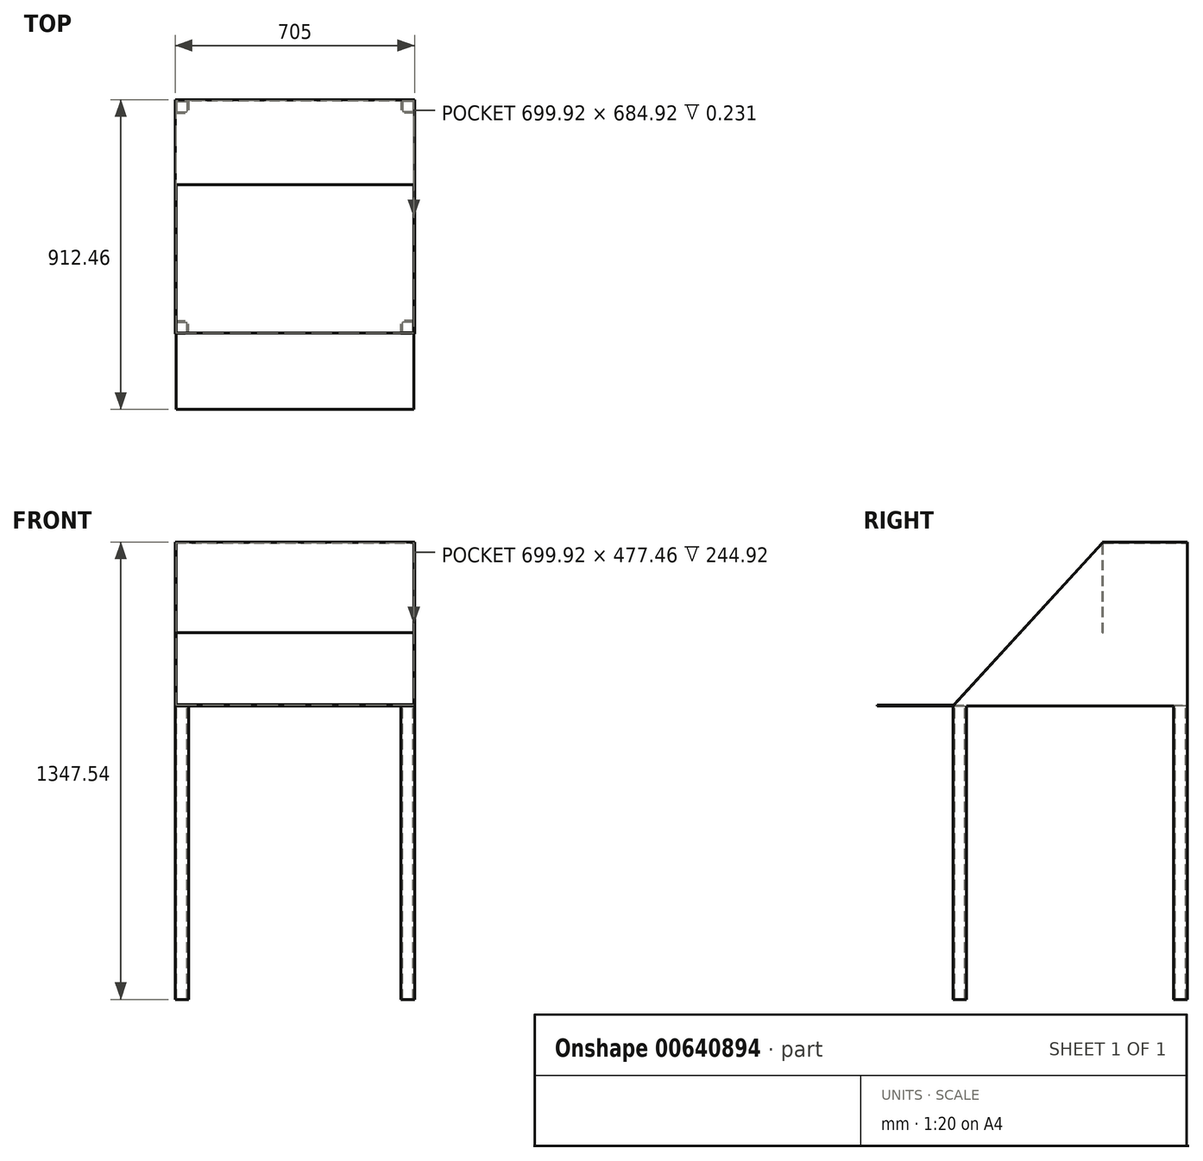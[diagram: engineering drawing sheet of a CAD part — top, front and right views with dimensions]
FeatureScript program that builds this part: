
annotation { "Feature Type Name" : "Feature", "Feature Type Description" : "" }
export const myFeature = defineFeature(function(context is Context, id is Id, definition is map)
    precondition{}
    {
        {
            var Q0;
            Q0=qCreatedBy(makeId("Front.planeOp"),FACE);
            var sketch = newSketch(context, id + "F0", { "sketchPlane" : qUnion([Q0])});
            skLineSegment(sketch, "E0.bottom", {"start": v(-352.5, 240) * mm, "end": v(352.5, 240) * mm});
            skLineSegment(sketch, "E0.top", {"start": v(-352.5, -240) * mm, "end": v(352.5, -240) * mm});
            skLineSegment(sketch, "E0.left", {"start": v(-352.5, 240) * mm, "end": v(-352.5, -240) * mm});
            skLineSegment(sketch, "E0.right", {"start": v(352.5, 240) * mm, "end": v(352.5, -240) * mm});
            skLineSegment(sketch, "E1", {"start": v(0, 1139.42) * mm, "end": v(0, -1506.63) * mm, "construction": true});
            skLineSegment(sketch, "E2", {"start": v(-1328.68, 0) * mm, "end": v(1394.06, 0) * mm, "construction": true});
            skSolve(sketch);
        }
        {
            var Q0;
            Q0 = qSketchRegion(id + "F0", true);
            extrude(context, id + "F1", {"entities" : qUnion([Q0]), "depth" : 690 * mm, "offsetDistance" : 25.4 * mm});
        }
        {
            var Q0;
            Q0=makeQuery(id+"F1.opExtrude","SWEPT_FACE",FACE,{"disambiguationData":[OSD([sQuery(id+"F0.wireOp",EDGE,"E0.bottom")])]});
            var sketch = newSketch(context, id + "F2", { "sketchPlane" : qUnion([Q0])});
            skLineSegment(sketch, "E3.bottom", {"start": v(-352.5, 0) * mm, "end": v(352.5, 0) * mm});
            skLineSegment(sketch, "E3.top", {"start": v(-352.5, -250) * mm, "end": v(352.5, -250) * mm});
            skLineSegment(sketch, "E3.left", {"start": v(-352.5, 0) * mm, "end": v(-352.5, -250) * mm});
            skLineSegment(sketch, "E3.right", {"start": v(352.5, 0) * mm, "end": v(352.5, -250) * mm});
            skSolve(sketch);
        }
        {
            var Q0;
            Q0=makeQuery(id+"F1.opExtrude","SWEPT_FACE",FACE,{"disambiguationData":[OSD([sQuery(id+"F0.wireOp",EDGE,"E0.right")])]});
            var sketch = newSketch(context, id + "F3", { "sketchPlane" : qUnion([Q0])});
            skLineSegment(sketch, "E4", {"start": v(-250, 240) * mm, "end": v(-690, -240) * mm});
            skLineSegment(sketch, "E5", {"start": v(-690, -240) * mm, "end": v(0, -240) * mm});
            skLineSegment(sketch, "E6", {"start": v(0, -240) * mm, "end": v(0, 240) * mm});
            skLineSegment(sketch, "E7", {"start": v(0, 240) * mm, "end": v(-250, 240) * mm});
            skSolve(sketch);
        }
        {
            var Q0;
            Q0=makeQuery(id+"F1.opExtrude","SWEPT_FACE",FACE,{"disambiguationData":[OSD([sQuery(id+"F0.wireOp",EDGE,"E0.bottom")])]});
            shell(context, id + "F4", {"entities" : qUnion([Q0]), "thickness" : 2.54 * mm});
        }
        {
            var Q0;
            {var subQ0=sQuery(id+"F3.wireOp",EDGE,"E4");Q0=makeQuery(id+"F3.imprint","IMPRINT",FACE,{"disambiguationData":[TD([[makeQuery(id+"F3.imprint","IMPRINT",EDGE,{"derivedFrom":subQ0}),-1.0]])]});}
            var Q1;
            Q1=makeQuery(id+"F1.opExtrude","SWEPT_FACE",FACE,{"disambiguationData":[OSD([sQuery(id+"F0.wireOp",EDGE,"E0.left")])]});
            extrude(context, id + "F5", {"entities" : qUnion([Q0]), "operationType" : NewBodyOperationType.REMOVE, "endBound" : BoundingType.UP_TO_SURFACE, "oppositeDirection" : true, "depth" : 25.4 * mm, "endBoundEntityFace" : qUnion([Q1]), "offsetDistance" : 25.4 * mm});
        }
        {
            var Q0;
            Q0=makeQuery(id+"F2.imprint","IMPRINT",FACE,{"disambiguationData":[TD([[makeQuery(id+"F2.imprint","IMPRINT",EDGE,{"derivedFrom":sQuery(id+"F2.wireOp",EDGE,"E3.bottom")}),-1.0]])]});
            extrude(context, id + "F6", {"entities" : qUnion([Q0]), "operationType" : NewBodyOperationType.ADD, "depth" : 2.54 * mm, "offsetDistance" : 25.4 * mm});
        }
        {
            var Q0;
            Q0=makeQuery(id+"F6.opExtrude","CAP_FACE",FACE,{"disambiguationData":[OSD([sQuery(id+"F2.wireOp",EDGE,"E3.bottom"),sQuery(id+"F2.wireOp",EDGE,"E3.top"),sQuery(id+"F2.wireOp",EDGE,"E3.left"),sQuery(id+"F2.wireOp",EDGE,"E3.right")])],"isStart":true});
            var sketch = newSketch(context, id + "F7", { "sketchPlane" : qUnion([Q0])});
            skLineSegment(sketch, "E8.bottom", {"start": v(-349.96, 250) * mm, "end": v(349.96, 250) * mm});
            skLineSegment(sketch, "E8.top", {"start": v(-349.96, 247.46) * mm, "end": v(349.96, 247.46) * mm});
            skLineSegment(sketch, "E8.left", {"start": v(-349.96, 250) * mm, "end": v(-349.96, 247.46) * mm});
            skLineSegment(sketch, "E8.right", {"start": v(349.96, 250) * mm, "end": v(349.96, 247.46) * mm});
            skSolve(sketch);
        }
        {
            var Q0;
            Q0 = qSketchRegion(id + "F7", true);
            extrude(context, id + "F8", {"entities" : qUnion([Q0]), "operationType" : NewBodyOperationType.ADD, "depth" : 265 * mm, "offsetDistance" : 25.4 * mm});
        }
        {
            var Q0;
            Q0=makeQuery(id+"F1.opExtrude","SWEPT_FACE",FACE,{"disambiguationData":[OSD([sQuery(id+"F0.wireOp",EDGE,"E0.top")])]});
            var sketch = newSketch(context, id + "F9", { "sketchPlane" : qUnion([Q0])});
            skLineSegment(sketch, "E9.bottom", {"start": v(-352.5, 690) * mm, "end": v(-312.5, 690) * mm});
            skLineSegment(sketch, "E9.top", {"start": v(-352.5, 650) * mm, "end": v(-312.5, 650) * mm});
            skLineSegment(sketch, "E9.left", {"start": v(-352.5, 690) * mm, "end": v(-352.5, 650) * mm});
            skLineSegment(sketch, "E9.right", {"start": v(-312.5, 690) * mm, "end": v(-312.5, 650) * mm});
            skLineSegment(sketch, "E10.bottom", {"start": v(-352.5, 0) * mm, "end": v(-312.5, 0) * mm});
            skLineSegment(sketch, "E10.top", {"start": v(-352.5, 40) * mm, "end": v(-312.5, 40) * mm});
            skLineSegment(sketch, "E10.left", {"start": v(-352.5, 0) * mm, "end": v(-352.5, 40) * mm});
            skLineSegment(sketch, "E10.right", {"start": v(-312.5, 0) * mm, "end": v(-312.5, 40) * mm});
            skLineSegment(sketch, "E11.bottom", {"start": v(352.5, 0) * mm, "end": v(312.5, 0) * mm});
            skLineSegment(sketch, "E11.top", {"start": v(352.5, 40) * mm, "end": v(312.5, 40) * mm});
            skLineSegment(sketch, "E11.left", {"start": v(352.5, 0) * mm, "end": v(352.5, 40) * mm});
            skLineSegment(sketch, "E11.right", {"start": v(312.5, 0) * mm, "end": v(312.5, 40) * mm});
            skLineSegment(sketch, "E12.bottom", {"start": v(352.5, 690) * mm, "end": v(312.5, 690) * mm});
            skLineSegment(sketch, "E12.top", {"start": v(352.5, 650) * mm, "end": v(312.5, 650) * mm});
            skLineSegment(sketch, "E12.left", {"start": v(352.5, 690) * mm, "end": v(352.5, 650) * mm});
            skLineSegment(sketch, "E12.right", {"start": v(312.5, 690) * mm, "end": v(312.5, 650) * mm});
            skLineSegment(sketch, "E13.0", {"start": v(-347.5, 685) * mm, "end": v(-317.5, 685) * mm});
            skLineSegment(sketch, "E13.1", {"start": v(-347.5, 685) * mm, "end": v(-347.5, 655) * mm});
            skLineSegment(sketch, "E13.2", {"start": v(-347.5, 655) * mm, "end": v(-317.5, 655) * mm});
            skLineSegment(sketch, "E13.3", {"start": v(-317.5, 685) * mm, "end": v(-317.5, 655) * mm});
            skLineSegment(sketch, "E14.0", {"start": v(-347.5, 35) * mm, "end": v(-317.5, 35) * mm});
            skLineSegment(sketch, "E14.1", {"start": v(-347.5, 5) * mm, "end": v(-347.5, 35) * mm});
            skLineSegment(sketch, "E14.2", {"start": v(-347.5, 5) * mm, "end": v(-317.5, 5) * mm});
            skLineSegment(sketch, "E14.3", {"start": v(-317.5, 5) * mm, "end": v(-317.5, 35) * mm});
            skLineSegment(sketch, "E15.0", {"start": v(347.5, 35) * mm, "end": v(317.5, 35) * mm});
            skLineSegment(sketch, "E15.1", {"start": v(347.5, 5) * mm, "end": v(347.5, 35) * mm});
            skLineSegment(sketch, "E15.2", {"start": v(347.5, 5) * mm, "end": v(317.5, 5) * mm});
            skLineSegment(sketch, "E15.3", {"start": v(317.5, 5) * mm, "end": v(317.5, 35) * mm});
            skLineSegment(sketch, "E16.0", {"start": v(347.5, 685) * mm, "end": v(317.5, 685) * mm});
            skLineSegment(sketch, "E16.1", {"start": v(347.5, 685) * mm, "end": v(347.5, 655) * mm});
            skLineSegment(sketch, "E16.2", {"start": v(347.5, 655) * mm, "end": v(317.5, 655) * mm});
            skLineSegment(sketch, "E16.3", {"start": v(317.5, 685) * mm, "end": v(317.5, 655) * mm});
            skSolve(sketch);
        }
        {
            var Q0;
            Q0 = qSketchRegion(id + "F9", true);
            extrude(context, id + "F10", {"entities" : qUnion([Q0]), "operationType" : NewBodyOperationType.ADD, "depth" : 865 * mm, "offsetDistance" : 25.4 * mm});
        }
        {
            var Q0;
            Q0=makeQuery(id+"F4.opShell","OFFSET_FACE",FACE,{"disambiguationData":[OSD([sQuery(id+"F0.wireOp",EDGE,"E0.top")])]});
            var sketch = newSketch(context, id + "F11", { "sketchPlane" : qUnion([Q0])});
            skLineSegment(sketch, "E17.bottom", {"start": v(-349.96, -687.46) * mm, "end": v(349.96, -687.46) * mm});
            skLineSegment(sketch, "E17.top", {"start": v(-349.96, -912.46) * mm, "end": v(349.96, -912.46) * mm});
            skLineSegment(sketch, "E17.left", {"start": v(-349.96, -687.46) * mm, "end": v(-349.96, -912.46) * mm});
            skLineSegment(sketch, "E17.right", {"start": v(349.96, -687.46) * mm, "end": v(349.96, -912.46) * mm});
            skSolve(sketch);
        }
        {
            var Q0;
            Q0 = qSketchRegion(id + "F11", true);
            extrude(context, id + "F12", {"entities" : qUnion([Q0]), "operationType" : NewBodyOperationType.ADD, "oppositeDirection" : true, "depth" : 2.54 * mm, "offsetDistance" : 25.4 * mm});
        }
    });
